# Revit family: Trane_TVR_Indoor_Compact 4-way Cassette_4TVB0007(09,12,15)EF000AA(2nd DC)
name_source: partatom
category: Equipamento mecânico
units: mm (PartAtom-declared; Revit-internal decimal feet)

## family parameters
Com base no plano de trabalho = Não
Compartilhado = Não
Corte com vazios quando carregada = Não
Cota do conector redondo = Utilizar diâmetro
Número OmniClass = 23.75.00.00
Ponto de cálculo do ambiente = Não
Sempre na vertical = Sim
Tipo de parte = Normal
Título OmniClass = Climate Control (HVAC)

## types (4) — shared parameters
Condensation = air
Depth = 570  [stored 1.87008 ft]
Descrição = High efficiency air cooled
Drain pipe = 32  [stored 0.104987 ft]
Fabricante = Trane
Gas = R410a
Gas pipe = 12.7  [stored 0.0416667 ft]
Height = 260
Installation = Indoor installation
Liquid pipe = 6.35  [stored 0.0208333 ft]
Machine material = grilles：ABS/HIPS
Maximum Fuse Amps = 15.000 A
Panel color = S1004
Power supply = 220-240V ~50/60Hz
Series = TVR ULTRA
URL = https://www.trane.com
Width = 630  [stored 2.06693 ft]
clearance access behind = 1000  [stored 3.28084 ft]
clearance access front = 1000  [stored 3.28084 ft]
clearance access left = 1000  [stored 3.28084 ft]
clearance access right = 1000  [stored 3.28084 ft]

## per-type parameters (varying)
| type | Air Flow | Cooling Capacity | Cooling Power Input | Heating Capacity | Heating Power Input | Minimum Circuit Amps | Net Weight |
| 4TVB0007EF000AA | 414/380/345/313/288/268/238m3/h | 2 kW | 35 W | 2 kW | 35 W | 0.430 A | 18.00 kg |
| 4TVB0009EF000AA | 414/380/345/313/288/268/238m3/h | 3 kW | 35 W | 3 kW | 35 W | 0.430 A | 18.00 kg |
| 4TVB0012EF000AA | 521/485/450/409/380/350/314m3/h | 4 kW | 40 W | 4 kW | 40 W | 0.480 A | 19.20 kg |
| 4TVB0015EF000AA | 521/485/450/409/380/350/314m3/h | 5 kW | 50 W | 5 kW | 50 W | 0.480 A | 19.20 kg |

note: column(s) folded — value = type name in every type: Modelo

note: [stored X ft] marks values corroborated as IEEE doubles in the binary element streams (Revit-internal decimal feet)

## geometry (parser evidence)
native form markers: Sweep x1
no freeform markers — native parametric forms only
